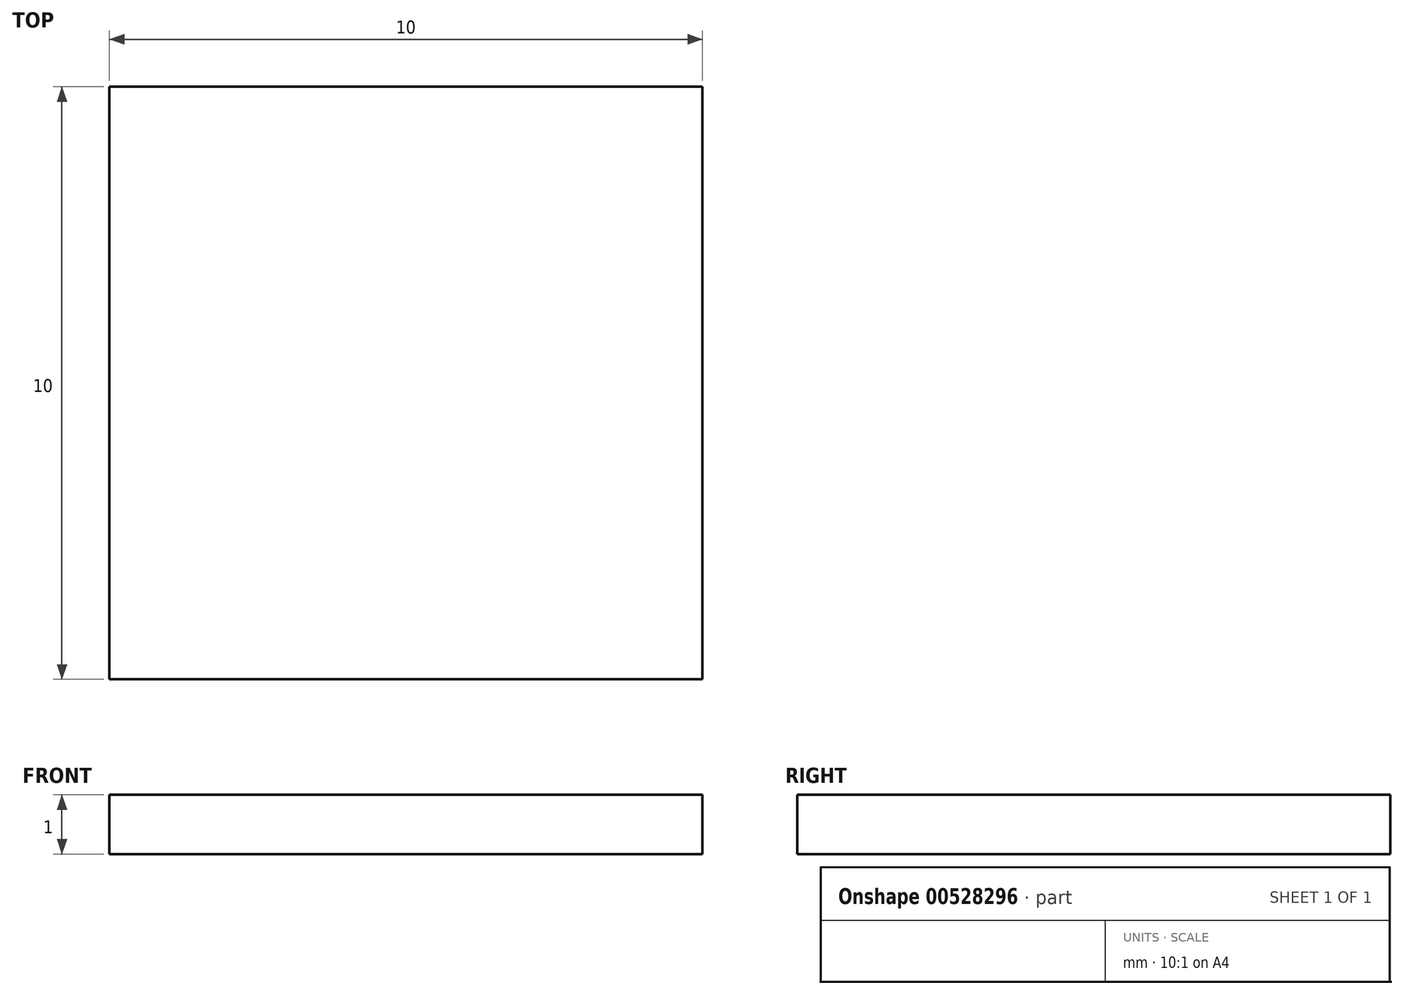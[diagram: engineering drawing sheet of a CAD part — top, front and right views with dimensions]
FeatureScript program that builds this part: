
annotation { "Feature Type Name" : "Feature", "Feature Type Description" : "" }
export const myFeature = defineFeature(function(context is Context, id is Id, definition is map)
    precondition{}
    {
        {
            var Q0;
            Q0=qCreatedBy(makeId("Top.planeOp"),FACE);
            var sketch = newSketch(context, id + "F0", { "sketchPlane" : qUnion([Q0])});
            skLineSegment(sketch, "E0.bottom", {"start": v(0, 0) * mm, "end": v(10, 0) * mm});
            skLineSegment(sketch, "E0.top", {"start": v(0, 10) * mm, "end": v(10, 10) * mm});
            skLineSegment(sketch, "E0.left", {"start": v(0, 0) * mm, "end": v(0, 10) * mm});
            skLineSegment(sketch, "E0.right", {"start": v(10, 0) * mm, "end": v(10, 10) * mm});
            skSolve(sketch);
        }
        {
            var Q0;
            Q0=makeQuery(id+"F0.imprint","IMPRINT",FACE,{"disambiguationData":[TD([[makeQuery(id+"F0.imprint","IMPRINT",EDGE,{"derivedFrom":sQuery(id+"F0.wireOp",EDGE,"E0.bottom")}),1.0]])]});
            extrude(context, id + "F1", {"entities" : qUnion([Q0]), "depth" : 1 * mm, "offsetDistance" : 25 * mm});
        }
    });
